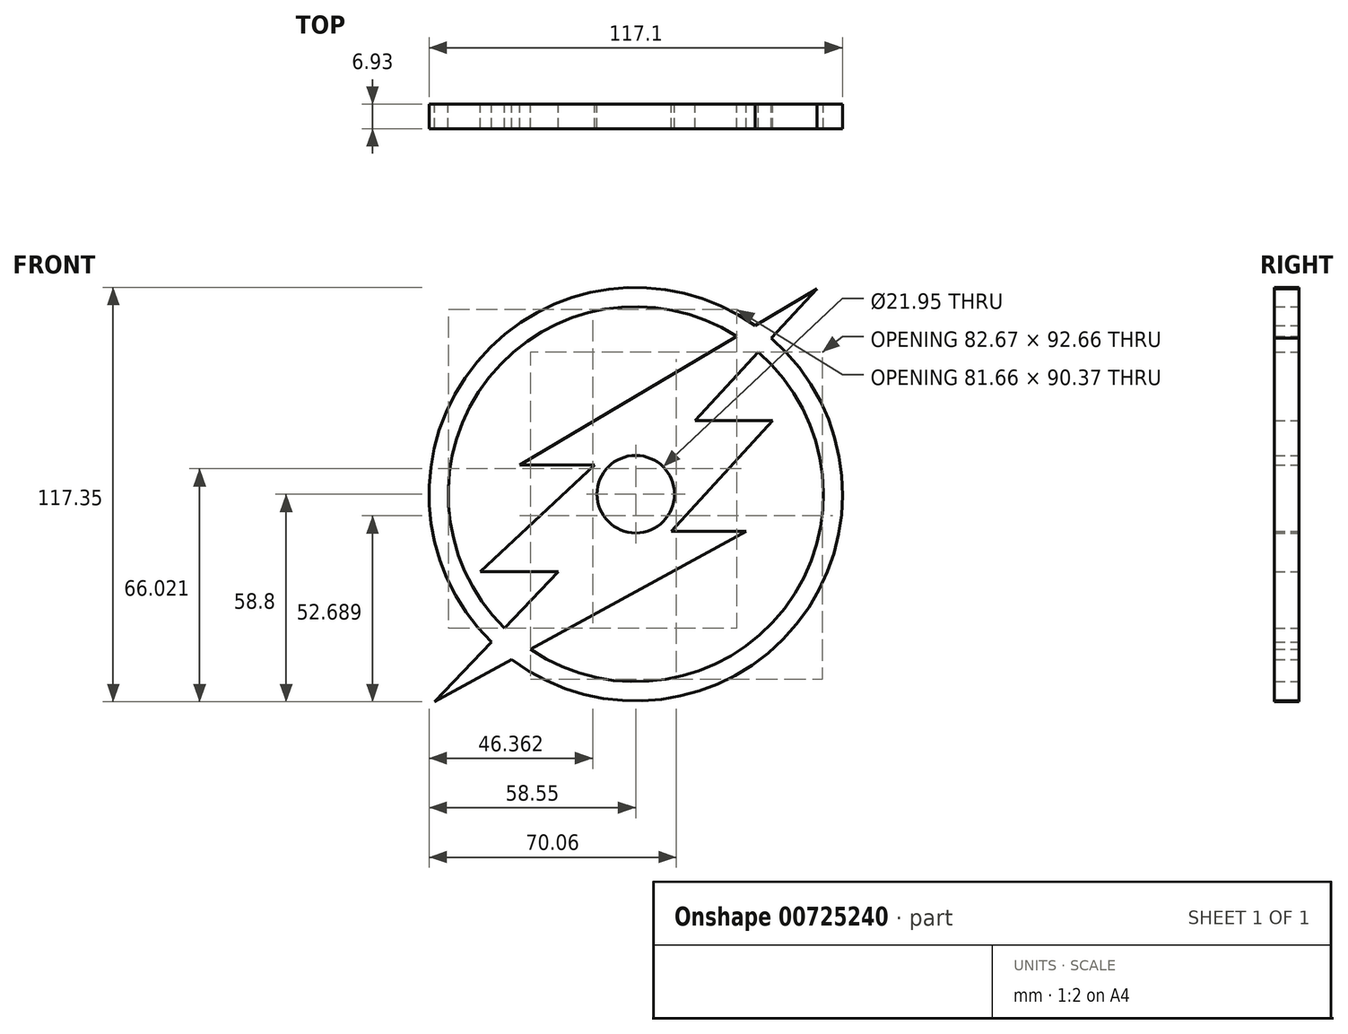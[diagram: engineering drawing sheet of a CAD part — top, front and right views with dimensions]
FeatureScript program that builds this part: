
annotation { "Feature Type Name" : "Feature", "Feature Type Description" : "" }
export const myFeature = defineFeature(function(context is Context, id is Id, definition is map)
    precondition{}
    {
        {
            var Q0;
            Q0=qCreatedBy(makeId("Front.planeOp"),FACE);
            var sketch = newSketch(context, id + "F0", { "sketchPlane" : qUnion([Q0])});
            skCircle(sketch, "E0", {"center": v(0, 0) * mm, "radius": 10.97 * mm});
            skLineSegment(sketch, "E1", {"start": v(16.8, 20.87) * mm, "end": v(51.3, 58.15) * mm});
            skLineSegment(sketch, "E2", {"start": v(51.3, 58.15) * mm, "end": v(-32.85, 8.34) * mm});
            skLineSegment(sketch, "E3", {"start": v(-44, -21.98) * mm, "end": v(-21.97, -21.98) * mm});
            skCircle(sketch, "E4", {"center": v(0, 0) * mm, "radius": 58.55 * mm});
            skCircle(sketch, "E5", {"center": v(0, 0) * mm, "radius": 53.12 * mm});
            skLineSegment(sketch, "E6", {"start": v(-32.85, 8.34) * mm, "end": v(-11.64, 8.34) * mm});
            skLineSegment(sketch, "E7", {"start": v(-11.64, 8.34) * mm, "end": v(-44, -21.98) * mm});
            skLineSegment(sketch, "E8", {"start": v(16.8, 20.87) * mm, "end": v(38.82, 20.87) * mm});
            skLineSegment(sketch, "E9", {"start": v(10.1, -10.53) * mm, "end": v(38.82, 20.87) * mm});
            skLineSegment(sketch, "E10", {"start": v(-21.97, -21.98) * mm, "end": v(-56.97, -58.8) * mm});
            skLineSegment(sketch, "E11", {"start": v(10.1, -10.53) * mm, "end": v(31.3, -10.53) * mm});
            skLineSegment(sketch, "E12", {"start": v(31.3, -10.53) * mm, "end": v(-56.97, -58.8) * mm});
            skSolve(sketch);
        }
        {
            var Q0;
            Q0 = qSketchRegion(id + "F0", true);
            var Q1;
            {var subQ1=sQuery(id+"F0.wireOp",EDGE,"FT9r5snU-KsSq-8QaD-tPcL-ZXkcWcEMV5bG");Q1=makeQuery(id+"F0.imprint","IMPRINT",FACE,{"disambiguationData":[TD([[makeQuery(id+"F0.imprint","IMPRINT",EDGE,{"derivedFrom":subQ1}),1.0]])]});}
            var Q2;
            {var subQ1=sQuery(id+"F0.wireOp",EDGE,"wtbwjk4S-n4gM-wiNL-7N9E-zhj8ZXDAe91g");Q2=makeQuery(id+"F0.imprint","IMPRINT",FACE,{"disambiguationData":[TD([[makeQuery(id+"F0.imprint","IMPRINT",EDGE,{"derivedFrom":subQ1}),1.0]])]});}
            var Q3;
            Q3=makeQuery(id+"F0.imprint","IMPRINT",FACE,{"disambiguationData":[TD([[makeQuery(id+"F0.imprint","IMPRINT",EDGE,{"derivedFrom":sQuery(id+"F0.wireOp",EDGE,"E0")}),-1.0]])]});
            extrude(context, id + "F1", {"entities" : qUnion([Q0, Q1, Q2, Q3]), "depth" : 6.93 * mm, "offsetDistance" : 25.4 * mm});
        }
    });
